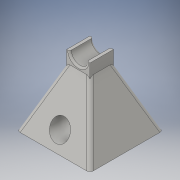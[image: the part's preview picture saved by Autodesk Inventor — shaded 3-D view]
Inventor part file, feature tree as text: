
AUTODESK INVENTOR PART (.ipt)
format: ipt  version: 2016 (Build 200138000, 138)  size: 146,944 bytes
history: native  units: in
note: dims shown in document units (in); Inventor stores cm internally (conversion verified against a paired STEP export)
features: sketch x4, plane x2, extrude x2, fillet x2, loft x1
ambient origin geometry x8: Origin, YZ Plane, XZ Plane, XY Plane, X Axis, Y Axis, Z Axis, Center Point
bodies: Solid1 (feature_tree)
feature tree (11):
  sketch  "Sketch1"  dims[d3=0.0in d4=90.0deg d5=0.0in d6=90.0deg]
  plane  "Work Plane1"
  loft  "Loft1"
  extrude  "Extrusion1"  Depth=0.0625in
  fillet  "Fillet3"  Radius=0.0312in
  fillet  "Fillet5"  Radius=0.625in
  plane  "Work Plane2"
  extrude  "Extrusion2"  [1 undecoded]
  sketch  "Sketch2"  dims[d11=0.0in d14=0.0625in d16=0.0312in d17=0.625in]
  sketch  "Sketch3"  dims[d20=1.0in d21=0.0in]
  sketch  "SketchForBottomHole"
note: 1 required parameter value undecoded (feature->parameter linkage not recoverable at this tier; creation-order binding heuristic only, values carry confidence <= 0.55)
